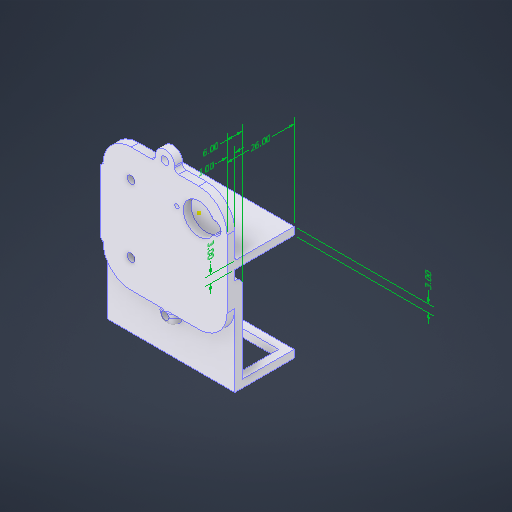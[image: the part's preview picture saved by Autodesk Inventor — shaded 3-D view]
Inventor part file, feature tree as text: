
AUTODESK INVENTOR PART (.ipt)
format: ipt  version: 2025.3 (Build 293356000, 356)  size: 415,232 bytes
history: native  units: in
note: dims shown in document units (in); Inventor stores cm internally (conversion verified against a paired STEP export)
features: extrude x12, sketch x10, other x6, fillet x5, direct_edit x3, move_body x3
ambient origin geometry x8: Origin, YZ Plane, XZ Plane, XY Plane, X Axis, Y Axis, Z Axis, Center Point
bodies: Solid1 (feature_tree)
feature tree (39):
  other  "Annotations"
  extrude  "Extrusion1"  Depth=0.0591in
  fillet  "Fillet1"  Radius=0.0591in
  fillet  "Fillet2"  Radius=0.9055in
  extrude  "Extrusion2"  Depth=1.0236in TaperAngle=0.0deg
  extrude  "Extrusion3"  Depth=0.0669in
  extrude  "Extrusion4"  Depth=1.172in
  fillet  "Fillet3"  Radius=1.0236in
  extrude  "Extrusion5"  Depth=0.1181in
  direct_edit  "Direct Edit1"
  extrude  "Extrusion6"  Depth=0.2378in
  extrude  "Extrusion7"  TaperAngle=0.0deg  [1 undecoded]
  direct_edit  "Direct Edit2"
  direct_edit  "Direct Edit3"
  sketch  "Sketch10"  dims[d25=0.0in d26=0.0in d27=0.6413in d28=0.1181in]
  extrude  "Extrusion8"  Depth=0.3937in TaperAngle=0.0deg
  extrude  "Extrusion9"  TaperAngle=0.0deg  [1 undecoded]
  extrude  "Extrusion10"  Depth=0.1181in
  extrude  "Extrusion11"  Depth=0.2362in TaperAngle=0.0deg
  fillet  "Fillet4"  [1 undecoded]
  extrude  "Extrusion12"  Depth=0.1181in
  fillet  "Fillet5"  Radius=0.1181in
  sketch  "Sketch1"  dims[d0=0.1181in d1=0.2953in d2=0.1181in d3=0.0in d4=0.0591in d5=0.0591in d11=0.9055in d12=0.0in]
  sketch  "Sketch2"  dims[d13=1.0236in d14=0.0in d17=1.0236in d18=0.0in]
  sketch  "Sketch3"  dims[d19=0.0315in d20=0.0669in]
  sketch  "Sketch7"  dims[d21=0.515in d22=1.172in d23=1.0236in d24=0.0in]
  sketch  "Sketch11"  dims[d29=0.4134in d30=0.2378in]
  sketch  "Sketch12"  dims[d31=0.3762in d32=0.0in d33=0.0in]
  sketch  "Sketch13"  dims[d34=0.1793in d35=0.3937in d36=0.0in]
  sketch  "Sketch14"  dims[d40=0.0in d41=0.0in d42=0.0394in d43=0.0in d44=0.0in d45=-0.0394in]
  sketch  "Sketch15"  dims[d50=0.1181in d51=0.0in d58=0.1181in d64=0.7874in d65=0.0in d66=45.0deg d67=0.1181in d68=0.1181in d69=135.0deg d70=0.7874in d71=0.0in d72=0.8504in d73=0.1181in d74=0.2362in d75=0.7874in d76=0.0in d77=0.1181in d78=0.1181in d79=0.7874in d80=0.0in d81=0.1181in d47=0.2862in d48=0.2809in d49=0.1181in d52=0.1865in d53=0.1902in d54=0.1181in d55=0.3167in d56=0.077in d57=0.1181in d59=0.0617in d60=0.0767in d61=0.2362in d62=0.158in d63=1.0236in]
  move_body  "Move1"
  move_body  "Move2"
  move_body  "Move3"
  other  "Linear Dimension 1"
  other  "Linear Dimension 2"
  other  "Linear Dimension 3"
  other  "Linear Dimension 4"
  other  "Linear Dimension 5"
note: 3 required parameter values undecoded (feature->parameter linkage not recoverable at this tier; creation-order binding heuristic only, values carry confidence <= 0.55)
